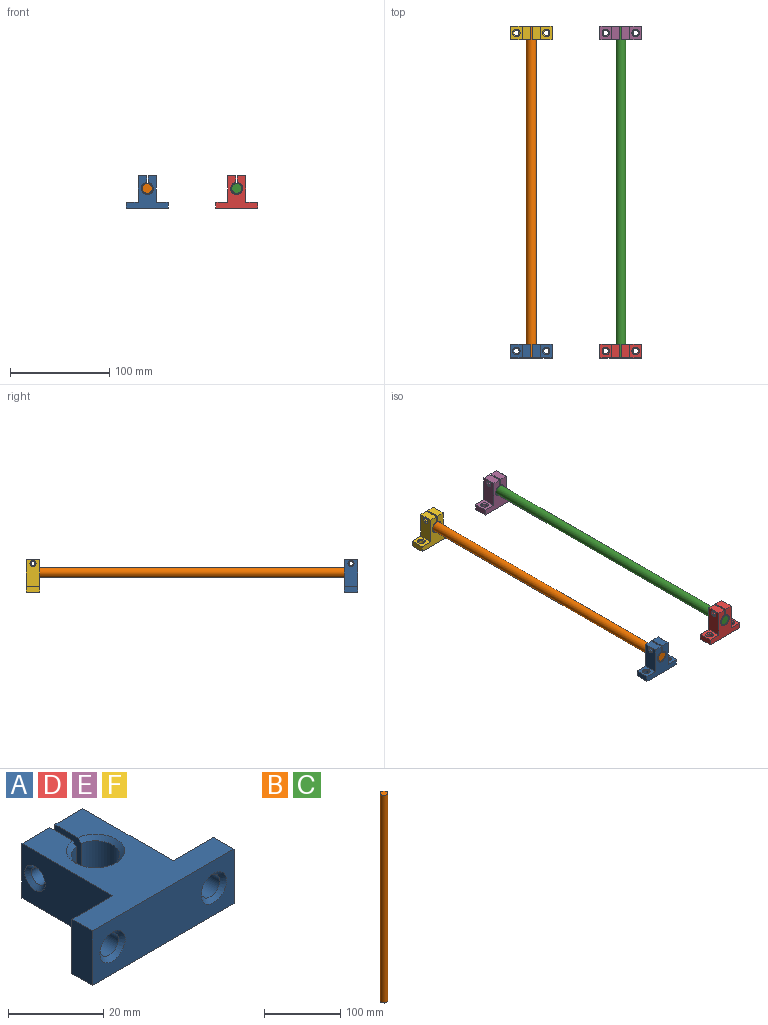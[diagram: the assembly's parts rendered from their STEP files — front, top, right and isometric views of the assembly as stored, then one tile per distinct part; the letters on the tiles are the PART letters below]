
ASSEMBLY  parts=6 mates=5
PART A: 28 faces, bbox 42x32.8x14 mm
  f0: cone r=3mm half-angle=45deg, axis (1,0,0), area 26.7mm2, adj f1,f2
  f1: cylinder r=2.5mm len=5mm, axis (-1,0,0), area 62.8mm2, adj f0,f21
  f2: plane 26.8x14mm, normal (1,0,0), area 336.7mm2, adj f0,f8,f10,f19,f24
  f3: cone r=3.25mm half-angle=45deg, axis (0,1,0), area 28.9mm2, adj f4,f5
  f4: cylinder r=2.75mm len=5.5mm, axis (0,1,0), area 69.1mm2, adj f3,f14
  f5: plane 14x12mm, normal (0,1,0), area 123.8mm2, adj f3,f10,f17,f19,f27
  f6: cone r=3.25mm half-angle=45deg, axis (0,1,0), area 28.9mm2, adj f7,f8
  f7: cylinder r=2.75mm len=5.5mm, axis (0,1,0), area 69.1mm2, adj f6,f12
  f8: plane 14x12mm, normal (0,1,0), area 123.8mm2, adj f2,f6,f10,f19,f26
  f9: cone r=5.6mm half-angle=45deg, axis (0,0,-1), area 47.6mm2, adj f10,f11,f20,f25
  f10: plane 42x32.8mm, normal (0,0,-1), area 607.4mm2, adj f2,f5,f8,f9,f11,f13,f17,f20
  f11: plane 14x7.76mm, normal (-1,0,0), area 94.4mm2, adj f9,f10,f18,f19,f22,f24,f25
  f12: cone r=3.25mm half-angle=45deg, axis (0,-1,0), area 28.9mm2, adj f7,f13
  f13: plane 42x14mm, normal (0,-1,0), area 499.6mm2, adj f10,f12,f14,f19,f26,f27
  f14: cone r=3.25mm half-angle=45deg, axis (0,-1,0), area 28.9mm2, adj f4,f13
  f15: cone r=2.55mm half-angle=45deg, axis (-1,0,0), area 22.7mm2, adj f16,f17
  f16: cylinder r=2.05mm len=7.25mm, axis (1,0,0), area 93.4mm2, adj f15,f20
  f17: plane 26.8x14mm, normal (-1,0,0), area 346mm2, adj f5,f10,f15,f19,f23
  f18: cone r=5.6mm half-angle=45deg, axis (0,0,1), area 47.6mm2, adj f11,f19,f20,f25
  f19: plane 42x32.8mm, normal (0,0,1), area 607.4mm2, adj f2,f5,f8,f11,f13,f17,f18,f20
  f20: plane 14x7.76mm, normal (1,0,0), area 94.4mm2, adj f9,f10,f16,f18,f19,f23,f25
  f21: plane 5x5mm, normal (1,0,0), area 6.4mm2, adj f1,f22
  f22: cylinder r=2.05mm len=4.1mm, axis (1,0,0), area 41.9mm2, adj f11,f21
  f23: plane 14x8.25mm, normal (0,1,0), area 115.5mm2, adj f10,f17,f19,f20
  f24: plane 14x8.25mm, normal (0,1,0), area 115.5mm2, adj f2,f10,f11,f19
  f25: cylinder r=5.1mm len=12mm, axis (0,0,1), area 366.5mm2, adj f9,f11,f18,f20
  f26: plane 14x6mm, normal (1,0,0), area 84mm2, adj f8,f10,f13,f19
  f27: plane 14x6mm, normal (-1,0,0), area 84mm2, adj f5,f10,f13,f19
PART B: 3 faces, bbox 10x10x334 mm
  f0: cylinder r=5mm len=334mm, axis (0,0,-1), area 10492.9mm2, adj f1,f2
  f1: plane 10x10mm, normal (0,0,1), area 78.5mm2, adj f0
  f2: plane 10x10mm, normal (0,0,-1), area 78.5mm2, adj f0
PART C: same geometry as B
PART D: same geometry as A
PART E: same geometry as A
PART F: same geometry as A
PLACE A rot(axis=(1,0,0),90deg) t=(3.4,-333.47,34.53)mm
PLACE B rot(axis=(-1,0,0),90deg) t=(-43.6,-340.47,28.84)mm
PLACE C rot(axis=(-1,0,0),90deg) t=(46.4,-340.47,28.84)mm
PLACE D rot(axis=(1,0,0),90deg) t=(93.4,-333.47,34.53)mm
PLACE E rot(axis=(1,0,0),90deg) t=(93.4,-13.47,34.53)mm
PLACE F rot(axis=(1,0,0),90deg) t=(3.4,-13.47,34.53)mm
MATE fastened D.f9 <-> C.f0  axis (0,-1,0) through (93.4,-340.47,35.13)mm
MATE fastened B.f0 <-> C.f1  axis (0,1,0) through (3.4,-6.47,35.13)mm
MATE fastened A.f9 <-> B.f0  axis (0,-1,0) through (3.4,-340.47,35.13)mm
MATE fastened F.f9 <-> C.f1  axis (0,1,0) through (3.4,-6.47,35.13)mm
MATE fastened E.f9 <-> C.f0  axis (0,1,0) through (93.4,-6.47,35.13)mm
